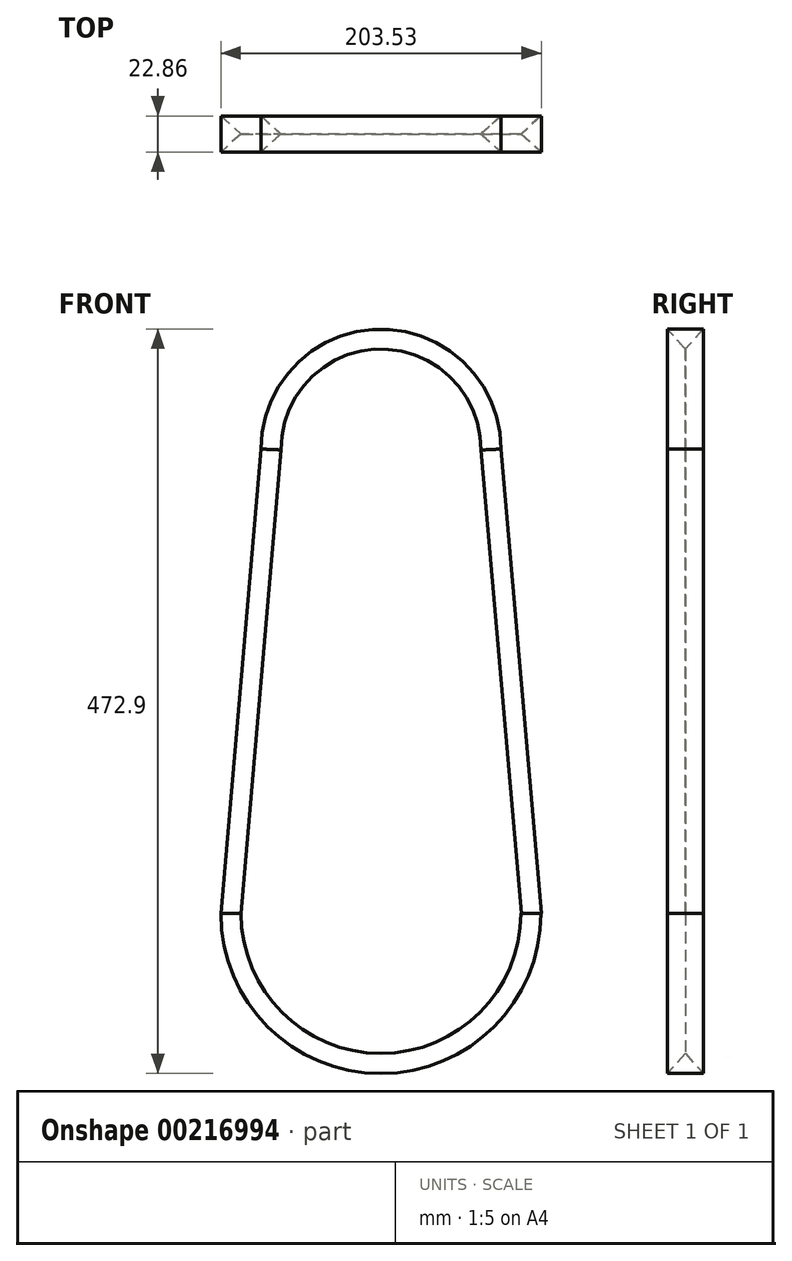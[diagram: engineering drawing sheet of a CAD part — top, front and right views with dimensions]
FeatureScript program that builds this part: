
annotation { "Feature Type Name" : "Feature", "Feature Type Description" : "" }
export const myFeature = defineFeature(function(context is Context, id is Id, definition is map)
    precondition{}
    {
        {
            var Q0;
            Q0=qCreatedBy(makeId("Front.planeOp"),FACE);
            var sketch = newSketch(context, id + "F0", { "sketchPlane" : qUnion([Q0])});
            skLineSegment(sketch, "E0", {"start": v(0, 0) * mm, "end": v(0, 349.25) * mm});
            skArc(sketch, "E1", {"start": v(-100.53, 14.7) * mm, "mid": v(-3.65, -101.53) * mm, "end": v(101.33, 7.45) * mm});
            skLineSegment(sketch, "E2", {"start": v(-101.6, 0) * mm, "end": v(-100.53, 14.7) * mm});
            skLineSegment(sketch, "E3", {"start": v(101.33, 7.45) * mm, "end": v(101.87, 0) * mm});
            skLineSegment(sketch, "E4", {"start": v(101.54, 3.54) * mm, "end": v(101.87, 0) * mm});
            skPoint(sketch, "E5.orphan", {"position": v(76.2, 349.25) * mm});
            skPoint(sketch, "E6.orphan", {"position": v(-76.2, 349.25) * mm});
            skArc(sketch, "E7", {"start": v(76.2, 295.05) * mm, "mid": v(0, 371.25) * mm, "end": v(-76.2, 295.05) * mm});
            skLineSegment(sketch, "E8", {"start": v(-76.2, 295.05) * mm, "end": v(-101.6, 0) * mm});
            skLineSegment(sketch, "E9", {"start": v(76.2, 295.05) * mm, "end": v(101.87, 0) * mm});
            skPoint(sketch, "E10.start.orphan", {"position": v(-76.2, 270.51) * mm});
            skPoint(sketch, "E11.center.orphan", {"position": v(0, 270.51) * mm});
            skPoint(sketch, "E12.orphan", {"position": v(76.2, 270.51) * mm});
            skSolve(sketch);
        }
        {
            var Q0;
            Q0=qCreatedBy(makeId("Top.planeOp"),FACE);
            var sketch = newSketch(context, id + "F1", { "sketchPlane" : qUnion([Q0])});
            skLineSegment(sketch, "E13", {"start": v(-101.63, 0) * mm, "end": v(-101.63, -11.43) * mm});
            skLineSegment(sketch, "E14", {"start": v(-101.63, 0) * mm, "end": v(-101.63, 11.43) * mm});
            skLineSegment(sketch, "E15", {"start": v(-101.63, 11.43) * mm, "end": v(-88.85, 0) * mm});
            skLineSegment(sketch, "E16", {"start": v(-88.85, 0) * mm, "end": v(-101.63, -11.43) * mm});
            skSolve(sketch);
        }
        {
            var Q0;
            Q0=qCreatedBy(makeId("Front.planeOp"),FACE);
            var sketch = newSketch(context, id + "F2", { "sketchPlane" : qUnion([Q0])});
            skCircle(sketch, "E17", {"center": v(0, 0) * mm, "radius": 101.6 * mm});
            skSolve(sketch);
        }
        {
            var Q0;
            Q0=makeQuery(id+"F1.imprint","IMPRINT",FACE,{"disambiguationData":[TD([[makeQuery(id+"F1.imprint","IMPRINT",EDGE,{"derivedFrom":sQuery(id+"F1.wireOp",EDGE,"E13")}),1.0]])]});
            var Q1;
            Q1=sQuery(id+"F0.wireOp",EDGE,"E8");
            var Q2;
            Q2=sQuery(id+"F0.wireOp",EDGE,"E7");
            var Q3;
            Q3=sQuery(id+"F0.wireOp",EDGE,"E9");
            sweep(context, id + "F3", {"profiles" : qUnion([Q0]), "path" : qUnion([Q1, Q2, Q3])});
        }
        {
            var Q0;
            Q0=makeQuery(id+"F3.opSweep","CAP_FACE",FACE,{"disambiguationData":[OSD([sQuery(id+"F0.wireOp",VERTEX,"E10.end"),sQuery(id+"F1.wireOp",EDGE,"E13"),sQuery(id+"F1.wireOp",EDGE,"E14"),sQuery(id+"F1.wireOp",EDGE,"E15"),sQuery(id+"F1.wireOp",EDGE,"E16")])],"isStart":true});
            var Q1;
            Q1=sQuery(id+"F2.wireOp",EDGE,"E17");
            revolve(context, id + "F4", {"operationType" : NewBodyOperationType.ADD, "entities" : qUnion([Q0]), "axis" : qUnion([Q1]), "revolveType" : RevolveType.ONE_DIRECTION, "angle" : 180 * degree});
        }
    });
